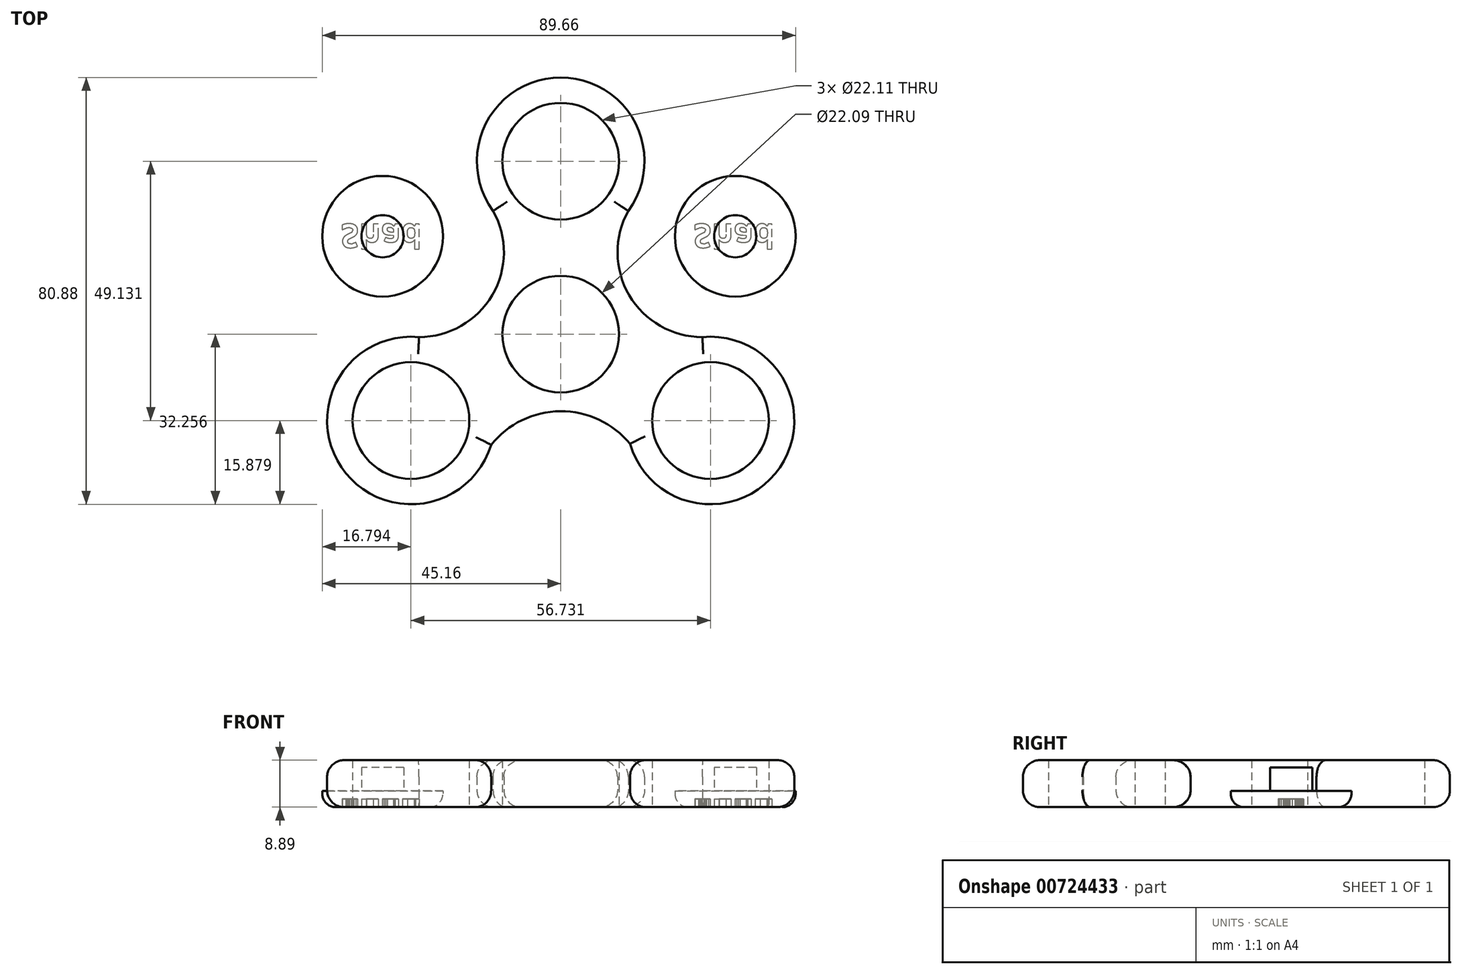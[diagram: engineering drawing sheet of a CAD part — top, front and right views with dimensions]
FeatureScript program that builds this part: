
annotation { "Feature Type Name" : "Feature", "Feature Type Description" : "" }
export const myFeature = defineFeature(function(context is Context, id is Id, definition is map)
    precondition{}
    {
        {
            var Q0;
            Q0=qCreatedBy(makeId("Top.planeOp"),FACE);
            var sketch = newSketch(context, id + "F0", { "sketchPlane" : qUnion([Q0])});
            skCircle(sketch, "E0", {"center": v(0, 61.7) * mm, "radius": 11.06 * mm});
            skCircle(sketch, "E1.1.0", {"center": v(-28.37, 12.58) * mm, "radius": 11.06 * mm});
            skCircle(sketch, "E1.2.0", {"center": v(28.37, 12.58) * mm, "radius": 11.06 * mm});
            skPoint(sketch, "E1.center", {"position": v(0, 28.96) * mm});
            skCircle(sketch, "E2", {"center": v(0, 28.96) * mm, "radius": 11.04 * mm});
            skArc(sketch, "E3", {"start": v(12.8, 52.32) * mm, "mid": v(0, 77.58) * mm, "end": v(-12.8, 52.32) * mm});
            skArc(sketch, "E4", {"start": v(-26.83, 28.38) * mm, "mid": v(-41.56, 3.75) * mm, "end": v(-13.17, 7.97) * mm});
            skArc(sketch, "E5", {"start": v(13.12, 8.14) * mm, "mid": v(41.51, 3.68) * mm, "end": v(26.83, 28.38) * mm});
            skArc(sketch, "E6", {"start": v(-26.83, 28.38) * mm, "mid": v(-12.5, 37.21) * mm, "end": v(-13.87, 54) * mm});
            skArc(sketch, "E7.MirrorCS", {"start": v(26.83, 28.38) * mm, "mid": v(12.5, 37.21) * mm, "end": v(13.87, 54) * mm});
            skArc(sketch, "E8", {"start": v(16.22, 2.35) * mm, "mid": v(0.13, 14.33) * mm, "end": v(-16.08, 2.52) * mm});
            skSolve(sketch);
        }
        {
            var Q0;
            Q0=qSketchRegion(id+"F0",true);
            extrude(context, id + "F1", {"entities" : qUnion([Q0]), "depth" : 8.9 * mm, "offsetDistance" : 25.4 * mm});
        }
        {
            var Q0;
            Q0=makeQuery(id+"F1.opExtrude","CAP_EDGE",EDGE,{"disambiguationData":[OSD([sQuery(id+"F0.wireOp",EDGE,"E8")])],"isStart":false});
            var Q1;
            Q1=makeQuery(id+"F1.opExtrude","CAP_EDGE",EDGE,{"disambiguationData":[OSD([sQuery(id+"F0.wireOp",EDGE,"E4")])],"isStart":false});
            var Q2;
            Q2=makeQuery(id+"F1.opExtrude","CAP_EDGE",EDGE,{"disambiguationData":[OSD([sQuery(id+"F0.wireOp",EDGE,"E6")])],"isStart":false});
            var Q3;
            Q3=makeQuery(id+"F1.opExtrude","CAP_EDGE",EDGE,{"disambiguationData":[OSD([sQuery(id+"F0.wireOp",EDGE,"E3")])],"isStart":false});
            var Q4;
            Q4=makeQuery(id+"F1.opExtrude","CAP_EDGE",EDGE,{"disambiguationData":[OSD([sQuery(id+"F0.wireOp",EDGE,"E5")])],"isStart":false});
            var Q5;
            Q5=makeQuery(id+"F1.opExtrude","CAP_EDGE",EDGE,{"disambiguationData":[OSD([sQuery(id+"F0.wireOp",EDGE,"E7.MirrorCS")])],"isStart":false});
            var Q6;
            Q6=makeQuery(id+"F1.opExtrude","CAP_EDGE",EDGE,{"disambiguationData":[OSD([sQuery(id+"F0.wireOp",EDGE,"E7.MirrorCS")])],"isStart":true});
            var Q7;
            Q7=makeQuery(id+"F1.opExtrude","CAP_EDGE",EDGE,{"disambiguationData":[OSD([sQuery(id+"F0.wireOp",EDGE,"E3")])],"isStart":true});
            var Q8;
            Q8=makeQuery(id+"F1.opExtrude","CAP_EDGE",EDGE,{"disambiguationData":[OSD([sQuery(id+"F0.wireOp",EDGE,"E5")])],"isStart":true});
            var Q9;
            Q9=makeQuery(id+"F1.opExtrude","CAP_EDGE",EDGE,{"disambiguationData":[OSD([sQuery(id+"F0.wireOp",EDGE,"E8")])],"isStart":true});
            var Q10;
            Q10=makeQuery(id+"F1.opExtrude","CAP_EDGE",EDGE,{"disambiguationData":[OSD([sQuery(id+"F0.wireOp",EDGE,"E4")])],"isStart":true});
            var Q11;
            Q11=makeQuery(id+"F1.opExtrude","CAP_EDGE",EDGE,{"disambiguationData":[OSD([sQuery(id+"F0.wireOp",EDGE,"E6")])],"isStart":true});
            fillet(context, id + "F2", {"entities" : qUnion([Q0, Q1, Q2, Q3, Q4, Q5, Q6, Q7, Q8, Q9, Q10, Q11]), "radius" : 3.17 * mm, "tangentPropagation" : true, "allowEdgeOverflow" : false});
        }
        {
            var Q0;
            Q0=qCreatedBy(makeId("Top.planeOp"),FACE);
            var sketch = newSketch(context, id + "F3", { "sketchPlane" : qUnion([Q0])});
            skCircle(sketch, "E9", {"center": v(33.07, 47.5) * mm, "radius": 11.43 * mm});
            skSolve(sketch);
        }
        {
            var Q0;
            Q0=makeQuery(id+"F3.imprint","IMPRINT",FACE,{"disambiguationData":[TD([[makeQuery(id+"F3.imprint","IMPRINT",EDGE,{"derivedFrom":sQuery(id+"F3.wireOp",EDGE,"E9")}),1.0]])]});
            extrude(context, id + "F4", {"entities" : qUnion([Q0]), "depth" : 3.05 * mm, "offsetDistance" : 25.4 * mm});
        }
        {
            var Q0;
            Q0=makeQuery(id+"F4.opExtrude","CAP_FACE",FACE,{"disambiguationData":[OSD([sQuery(id+"F3.wireOp",EDGE,"E9")])],"isStart":false});
            var sketch = newSketch(context, id + "F5", { "sketchPlane" : qUnion([Q0])});
            skCircle(sketch, "E10", {"center": v(33.07, 47.5) * mm, "radius": 4 * mm});
            skSolve(sketch);
        }
        {
            var Q0;
            Q0=makeQuery(id+"F5.imprint","IMPRINT",FACE,{"disambiguationData":[TD([[makeQuery(id+"F5.imprint","IMPRINT",EDGE,{"derivedFrom":sQuery(id+"F5.wireOp",EDGE,"E10")}),1.0]])]});
            extrude(context, id + "F6", {"entities" : qUnion([Q0]), "operationType" : NewBodyOperationType.ADD, "depth" : 4.44 * mm, "offsetDistance" : 25.4 * mm});
        }
        {
            var Q0;
            Q0=makeQuery(id+"F4.opExtrude","CAP_EDGE",EDGE,{"disambiguationData":[OSD([sQuery(id+"F3.wireOp",EDGE,"E9")])],"isStart":true});
            fillet(context, id + "F7", {"entities" : qUnion([Q0]), "radius" : 2.54 * mm, "tangentPropagation" : true, "allowEdgeOverflow" : false});
        }
        {
            var Q0;
            Q0=makeQuery(id+"F4.opExtrude","CAP_FACE",FACE,{"disambiguationData":[OSD([sQuery(id+"F3.wireOp",EDGE,"E9")])],"isStart":true});
            var sketch = newSketch(context, id + "F8", { "sketchPlane" : qUnion([Q0])});
            skText(sketch, "E11", { "text": "Shad", "fontName": "OpenSans-Bold.ttf"});
            const initialGuessF8  = {"E11": [0.02513, -0.04983, 1, 0, 0.00453]};
            skSetInitialGuess(sketch, initialGuessF8);
            skSolve(sketch);
        }
        {
            var Q0;
            Q0=qSketchRegion(id+"F8",true);
            extrude(context, id + "F9", {"entities" : qUnion([Q0]), "operationType" : NewBodyOperationType.REMOVE, "oppositeDirection" : true, "depth" : 1.52 * mm, "offsetDistance" : 25.4 * mm});
        }
        {
            var Q0;
            Q0=makeQuery(id+"F4.opExtrude","SWEPT_BODY",BODY,{"disambiguationData":[OSD([sQuery(id+"F3.wireOp",EDGE,"E9")])]});
            transform(context, id + "F10", {"entities" : qUnion([Q0]), "transformType" : TransformType.TRANSLATION_3D, "dx" : -66.8 * mm, "dy" : 0 * mm, "dz" : 0 * mm, "makeCopy" : true});
        }
    });
